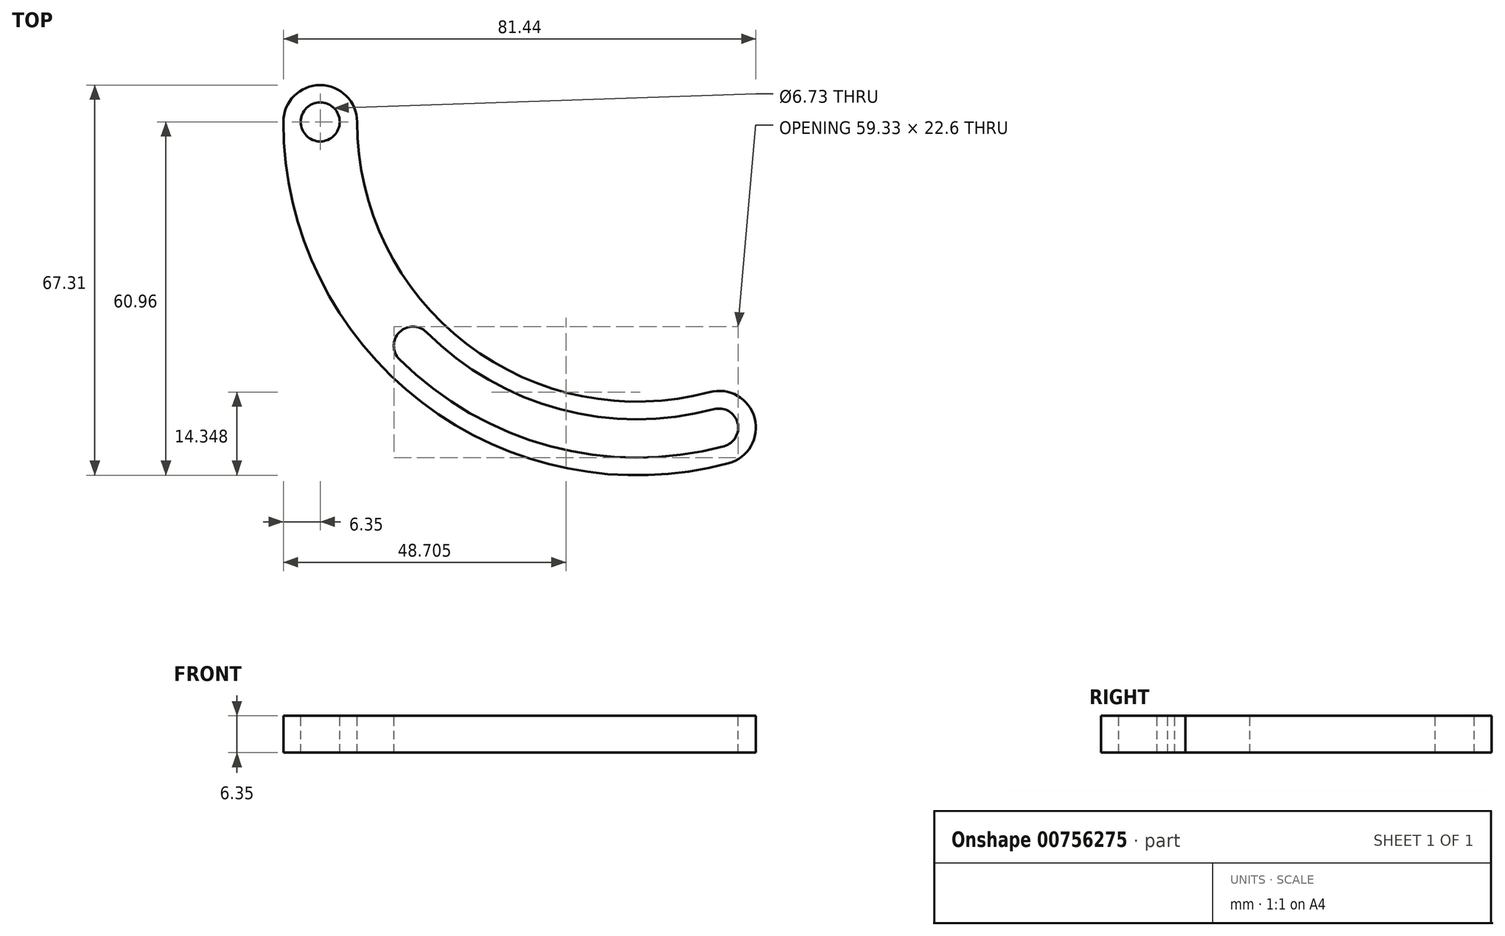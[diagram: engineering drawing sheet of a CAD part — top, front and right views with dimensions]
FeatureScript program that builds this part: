
annotation { "Feature Type Name" : "Feature", "Feature Type Description" : "" }
export const myFeature = defineFeature(function(context is Context, id is Id, definition is map)
    precondition{}
    {
        {
            var Q0;
            Q0=qCreatedBy(makeId("Top.planeOp"),FACE);
            var sketch = newSketch(context, id + "F0", { "sketchPlane" : qUnion([Q0])});
            skLineSegment(sketch, "E0", {"start": v(0, 0) * mm, "end": v(-54.61, 0) * mm});
            skLineSegment(sketch, "E1", {"start": v(-54.61, 0) * mm, "end": v(0, 0) * mm});
            skLineSegment(sketch, "E2", {"start": v(0, 0) * mm, "end": v(14.13, -52.75) * mm});
            skCircle(sketch, "E3", {"center": v(-54.61, 0) * mm, "radius": 3.37 * mm});
            skLineSegment(sketch, "E4", {"start": v(0, 0) * mm, "end": v(-38.62, -38.62) * mm});
            skCircle(sketch, "E5", {"center": v(-38.62, -38.62) * mm, "radius": 3.3 * mm});
            skCircle(sketch, "E6", {"center": v(14.13, -52.75) * mm, "radius": 3.3 * mm});
            skPoint(sketch, "E7", {"position": v(13.28, -49.56) * mm});
            skPoint(sketch, "E8", {"position": v(-36.28, -36.28) * mm});
            skArc(sketch, "E9", {"start": v(-36.28, -36.28) * mm, "mid": v(-13.28, -49.56) * mm, "end": v(13.28, -49.56) * mm});
            skLineSegment(sketch, "E10", {"start": v(-36.28, -36.28) * mm, "end": v(-40.95, -40.95) * mm});
            skLineSegment(sketch, "E11", {"start": v(13.28, -49.56) * mm, "end": v(14.99, -55.94) * mm});
            skArc(sketch, "E12", {"start": v(-40.95, -40.95) * mm, "mid": v(-14.99, -55.94) * mm, "end": v(14.99, -55.94) * mm});
            skLineSegment(sketch, "E13", {"start": v(0, 0) * mm, "end": v(-48.26, 0) * mm});
            skLineSegment(sketch, "E14", {"start": v(-48.26, 0) * mm, "end": v(0, 0) * mm});
            skLineSegment(sketch, "E15", {"start": v(0, 0) * mm, "end": v(12.5, -46.62) * mm});
            skArc(sketch, "E16", {"start": v(-48.26, 0) * mm, "mid": v(-29.38, -38.29) * mm, "end": v(12.5, -46.62) * mm});
            skLineSegment(sketch, "E17", {"start": v(0, 0) * mm, "end": v(15.78, -58.88) * mm});
            skLineSegment(sketch, "E18", {"start": v(0, 0) * mm, "end": v(-60.96, 0) * mm});
            skArc(sketch, "E19", {"start": v(-60.96, 0) * mm, "mid": v(-37.11, -48.36) * mm, "end": v(15.78, -58.88) * mm});
            skCircle(sketch, "E20", {"center": v(-54.61, 0) * mm, "radius": 6.35 * mm});
            skCircle(sketch, "E21", {"center": v(14.13, -52.75) * mm, "radius": 6.35 * mm});
            skSolve(sketch);
        }
        {
            var Q0;
            {var subQ0=sQuery(id+"F0.wireOp",EDGE,"E18");var subQ1=sQuery(id+"F0.wireOp",EDGE,"E3");var subQ2=makeQuery(id+"F0.imprint","INTERSECT",VERTEX,{"disambiguationData":[OD(0.0)],"derivedFrom":[subQ1,subQ0]});Q0=makeQuery(id+"F0.imprint","IMPRINT",FACE,{"disambiguationData":[TD([[makeQuery(id+"F0.imprint","IMPRINT",EDGE,{"disambiguationData":[TD([[subQ2,-1.0]])],"derivedFrom":subQ1}),-1.0]])]});}
            var Q1;
            {var subQ0=sQuery(id+"F0.wireOp",EDGE,"E18");var subQ1=sQuery(id+"F0.wireOp",EDGE,"E3");var subQ2=makeQuery(id+"F0.imprint","INTERSECT",VERTEX,{"disambiguationData":[OD(0.0)],"derivedFrom":[subQ1,subQ0]});Q1=makeQuery(id+"F0.imprint","IMPRINT",FACE,{"disambiguationData":[TD([[makeQuery(id+"F0.imprint","IMPRINT",EDGE,{"disambiguationData":[TD([[subQ2,1.0]])],"derivedFrom":subQ1}),-1.0]])]});}
            var Q2;
            {var subQ13=sQuery(id+"F0.wireOp",EDGE,"E19");Q2=makeQuery(id+"F0.imprint","IMPRINT",FACE,{"disambiguationData":[TD([[makeQuery(id+"F0.imprint","IMPRINT",EDGE,{"derivedFrom":subQ13}),1.0]])]});}
            var Q3;
            {var subQ1=sQuery(id+"F0.wireOp",EDGE,"E4");var subQ3=sQuery(id+"F0.wireOp",EDGE,"E16");var subQ4=makeQuery(id+"F0.imprint","INTERSECT",VERTEX,{"derivedFrom":[subQ1,subQ3]});Q3=makeQuery(id+"F0.imprint","IMPRINT",FACE,{"disambiguationData":[TD([[makeQuery(id+"F0.imprint","IMPRINT",EDGE,{"disambiguationData":[TD([[subQ4,-1.0]])],"derivedFrom":subQ3}),-1.0]])]});}
            var Q4;
            {var subQ0=sQuery(id+"F0.wireOp",EDGE,"E17");var subQ1=sQuery(id+"F0.wireOp",EDGE,"E6");var subQ2=makeQuery(id+"F0.imprint","INTERSECT",VERTEX,{"derivedFrom":[subQ1,sQuery(id+"F0.wireOp",EDGE,"E9"),subQ0]});Q4=makeQuery(id+"F0.imprint","IMPRINT",FACE,{"disambiguationData":[TD([[makeQuery(id+"F0.imprint","IMPRINT",EDGE,{"disambiguationData":[TD([[subQ2,1.0]])],"derivedFrom":subQ1}),-1.0]])]});}
            var Q5;
            {var subQ1=sQuery(id+"F0.wireOp",EDGE,"E9");var subQ3=sQuery(id+"F0.wireOp",EDGE,"E21");var subQ4=makeQuery(id+"F0.imprint","INTERSECT",VERTEX,{"derivedFrom":[subQ1,subQ3]});Q5=makeQuery(id+"F0.imprint","IMPRINT",FACE,{"disambiguationData":[TD([[makeQuery(id+"F0.imprint","IMPRINT",EDGE,{"disambiguationData":[TD([[subQ4,-1.0]])],"derivedFrom":subQ1}),1.0]])]});}
            var Q6;
            {var subQ1=sQuery(id+"F0.wireOp",EDGE,"E12");var subQ3=sQuery(id+"F0.wireOp",EDGE,"E21");var subQ4=makeQuery(id+"F0.imprint","INTERSECT",VERTEX,{"derivedFrom":[subQ1,subQ3]});Q6=makeQuery(id+"F0.imprint","IMPRINT",FACE,{"disambiguationData":[TD([[makeQuery(id+"F0.imprint","IMPRINT",EDGE,{"disambiguationData":[TD([[subQ4,-1.0]])],"derivedFrom":subQ1}),-1.0]])]});}
            extrude(context, id + "F1", {"entities" : qUnion([Q0, Q1, Q2, Q3, Q4, Q5, Q6]), "oppositeDirection" : true, "depth" : 6.35 * mm, "offsetDistance" : 25.4 * mm});
        }
    });
